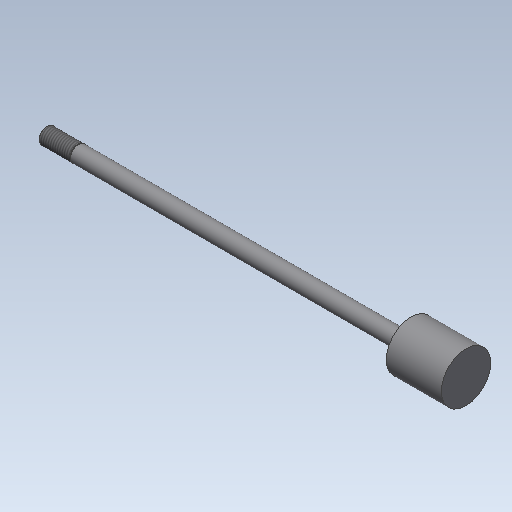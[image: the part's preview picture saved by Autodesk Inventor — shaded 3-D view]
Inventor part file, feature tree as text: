
AUTODESK INVENTOR PART (.ipt)
format: ipt  version: 2020 (Build 240168000, 168)  size: 154,624 bytes
history: native  units: in
note: dims shown in document units (in); Inventor stores cm internally (conversion verified against a paired STEP export)
features: other x84, revolve x3, sketch x3, thread x1
ambient origin geometry x8: Origin, YZ Plane, XZ Plane, XY Plane, X Axis, Y Axis, Z Axis, Center Point
bodies: Solid1 (feature_tree)
feature tree (91):
  revolve  "Revolution1"  Angle=360.0deg
  revolve  "Revolution2"  Angle=360.0deg
  thread  "Thread1"  [1 undecoded]
  revolve  "Revolution3"  [1 undecoded]
  other  "dia1_XY"
  other  "dia1_YZ"
  other  "dia1_ZX"
  other  "dia1_X"
  other  "dia1_Y"
  other  "dia1_Z"
  other  "dia1_Center"
  other  "dia12_XY"
  other  "dia12_YZ"
  other  "dia12_ZX"
  other  "dia12_X"
  other  "dia12_Y"
  other  "dia12_Z"
  other  "dia12_Center"
  other  "dia2_XY"
  other  "dia2_YZ"
  other  "dia2_ZX"
  other  "dia2_X"
  other  "dia2_Y"
  other  "dia2_Z"
  other  "dia2_Center"
  other  "dia22_XY"
  other  "dia22_YZ"
  other  "dia22_ZX"
  other  "dia22_X"
  other  "dia22_Y"
  other  "dia22_Z"
  other  "dia22_Center"
  other  "hh1_XY"
  other  "hh1_YZ"
  other  "hh1_ZX"
  other  "hh1_X"
  other  "hh1_Y"
  other  "hh1_Z"
  other  "hh1_Center"
  other  "hh2_XY"
  other  "hh2_YZ"
  other  "hh2_ZX"
  other  "hh2_X"
  other  "hh2_Y"
  other  "hh2_Z"
  other  "hh2_Center"
  other  "rl1_XY"
  other  "rl1_YZ"
  other  "rl1_ZX"
  other  "rl1_X"
  other  "rl1_Y"
  other  "rl1_Z"
  other  "rl1_Center"
  other  "rl2_XY"
  other  "rl2_YZ"
  other  "rl2_ZX"
  other  "rl2_X"
  other  "rl2_Y"
  other  "rl2_Z"
  other  "rl2_Center"
  other  "rod_cp_XY"
  other  "rod_cp_YZ"
  other  "rod_cp_ZX"
  other  "rod_cp_X"
  other  "rod_cp_Y"
  other  "rod_cp_Z"
  other  "rod_cp_Center"
  other  "thd1_XY"
  other  "thd1_YZ"
  other  "thd1_ZX"
  other  "thd1_X"
  other  "thd1_Y"
  other  "thd1_Z"
  other  "thd1_Center"
  other  "thd2_XY"
  other  "thd2_YZ"
  other  "thd2_ZX"
  other  "thd2_X"
  other  "thd2_Y"
  other  "thd2_Z"
  other  "thd2_Center"
  other  "to_rod_clevis_XY"
  other  "to_rod_clevis_YZ"
  other  "to_rod_clevis_ZX"
  other  "to_rod_clevis_X"
  other  "to_rod_clevis_Y"
  other  "to_rod_clevis_Z"
  other  "to_rod_clevis_Center"
  sketch  "Sketch_1"  dims[d0=360.0deg d1=360.0deg]
  sketch  "Sketch_3"  dims[d2=0.4787in d3=0.0in d4=360.0deg]
  sketch  "Sketch_30"  dims[d5=0.0in d6=0.0in d7=0.0in d8=0.0in d9=0.0in]
note: 2 required parameter values undecoded (feature->parameter linkage not recoverable at this tier; creation-order binding heuristic only, values carry confidence <= 0.55)
